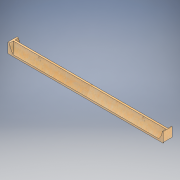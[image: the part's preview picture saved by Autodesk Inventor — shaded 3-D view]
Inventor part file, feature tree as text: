
AUTODESK INVENTOR PART (.ipt)
format: ipt  version: 2022.2 (Build 262287010, 287A)  size: 189,440 bytes
history: native  units: in
note: dims shown in document units (in); Inventor stores cm internally (conversion verified against a paired STEP export)
features: direct_edit x1, extrude x1, sketch x1, projected_geometry x1, other x1, revolve x1
ambient origin geometry x8: Origin, YZ Plane, XZ Plane, XY Plane, X Axis, Y Axis, Z Axis, Center Point
bodies: Solid1 (feature_tree)
feature tree (6):
  direct_edit  "Direct Edit1"
  extrude  "Extrusion1"  Depth=1.0in TaperAngle=0.0deg
  sketch  "Sketch1"  dims[d0=-1.2368in d1=1.0in d2=0.0in]
  projected_geometry  "Projected Loop1"
  other  "Upper Jamb (2) (1)"
  revolve  "Rotate1"  [1 undecoded]
note: 1 required parameter value undecoded (feature->parameter linkage not recoverable at this tier; creation-order binding heuristic only, values carry confidence <= 0.55)
